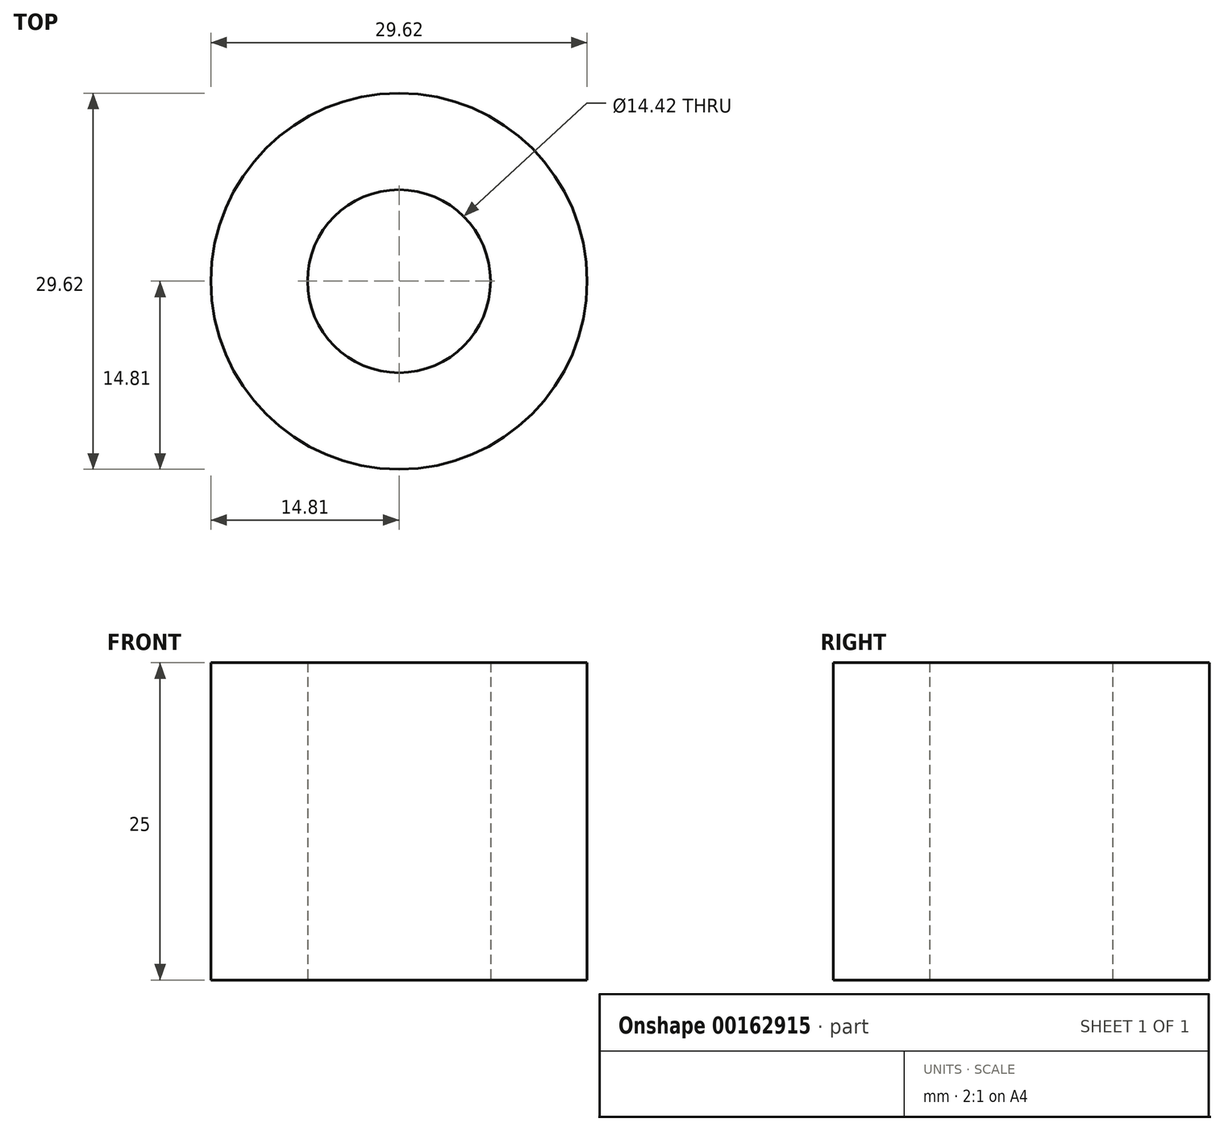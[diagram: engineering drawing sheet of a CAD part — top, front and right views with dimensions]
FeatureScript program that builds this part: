
annotation { "Feature Type Name" : "Feature", "Feature Type Description" : "" }
export const myFeature = defineFeature(function(context is Context, id is Id, definition is map)
    precondition{}
    {
        {
            var Q0;
            Q0=qCreatedBy(makeId("Top.planeOp"),FACE);
            var sketch = newSketch(context, id + "F0", { "sketchPlane" : qUnion([Q0])});
            skCircle(sketch, "E0", {"center": v(0, 0) * mm, "radius": 7.2 * mm});
            skCircle(sketch, "E1", {"center": v(0, 0) * mm, "radius": 14.81 * mm});
            skSolve(sketch);
        }
        {
            var Q0;
            Q0 = qSketchRegion(id + "F0", true);
            extrude(context, id + "F1", {"entities" : qUnion([Q0]), "depth" : 25 * mm});
        }
    });
